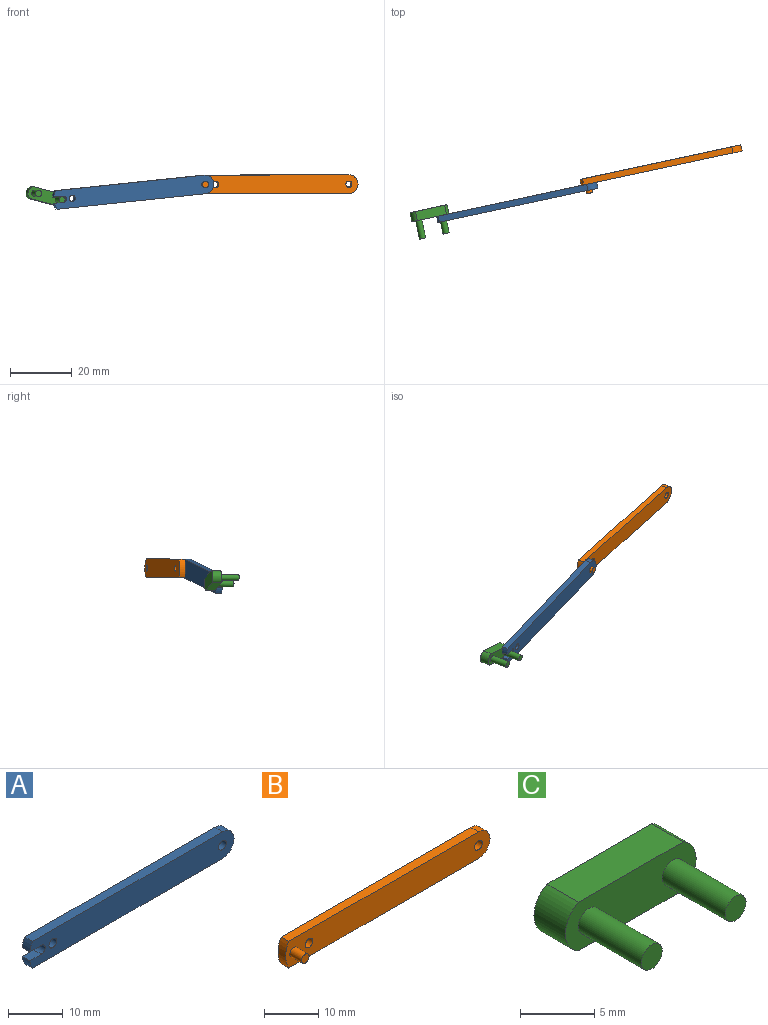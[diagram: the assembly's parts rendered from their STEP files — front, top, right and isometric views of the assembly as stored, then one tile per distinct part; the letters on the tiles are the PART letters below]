
ASSEMBLY  parts=3 mates=2
PART A: 12 faces, bbox 53x2x6 mm
  f0: cylinder r=1mm len=2mm, axis (0,1,0), area 6.3mm2, adj f1,f8,f10,f11
  f1: plane 3x2mm, normal (0,0,1), area 6mm2, adj f0,f2,f10,f11
  f2: cylinder r=6.08mm len=2mm, axis (0,1,0), area 4.3mm2, adj f1,f3,f10,f11
  f3: plane 49.29x2mm, normal (0,0,-1), area 98.6mm2, adj f2,f4,f10,f11
  f4: cylinder r=3mm len=6mm, axis (0,1,0), area 18.8mm2, adj f3,f5,f10,f11
  f5: plane 49.29x2mm, normal (0,0,1), area 98.6mm2, adj f4,f6,f10,f11
  f6: cylinder r=6.08mm len=2mm, axis (0,1,0), area 4.3mm2, adj f5,f8,f10,f11
  f7: cylinder r=1mm len=2mm, axis (0,1,0), area 12.6mm2, adj f10,f11
  f8: plane 3x2mm, normal (0,0,-1), area 6mm2, adj f0,f6,f10,f11
  f9: cylinder r=1mm len=2mm, axis (0,1,0), area 12.6mm2, adj f10,f11
  f10: plane 53x6mm, normal (0,-1,0), area 299.1mm2, adj f0,f1,f2,f3,f4,f5,f6,f7
  f11: plane 53x6mm, normal (0,1,0), area 299.1mm2, adj f0,f1,f2,f3,f4,f5,f6,f7
PART B: 10 faces, bbox 53.1x5x6 mm
  f0: cylinder r=6.08mm len=6mm, axis (0,1,0), area 12.5mm2, adj f1,f5,f6,f7
  f1: plane 49.29x2mm, normal (0,0,-1), area 98.6mm2, adj f0,f2,f6,f7
  f2: cylinder r=3mm len=6mm, axis (0,1,0), area 18.8mm2, adj f1,f5,f6,f7
  f3: cylinder r=1mm len=2mm, axis (0,1,0), area 12.6mm2, adj f6,f7
  f4: cylinder r=1mm len=2mm, axis (0,1,0), area 12.6mm2, adj f6,f7
  f5: plane 49.29x2mm, normal (0,0,1), area 98.6mm2, adj f0,f2,f6,f7
  f6: plane 53.08x6mm, normal (0,-1,0), area 303.7mm2, adj f0,f1,f2,f3,f4,f5,f8
  f7: plane 53.08x6mm, normal (0,1,0), area 306.8mm2, adj f0,f1,f2,f3,f4,f5
  f8: cylinder r=1mm len=3mm, axis (0,1,0), area 18.8mm2, adj f6,f9
  f9: plane 2x2mm, normal (0,-1,0), area 3.1mm2, adj f8
PART C: 10 faces, bbox 12.5x9x4 mm
  f0: plane 10x3mm, normal (0,0,-1), area 30mm2, adj f2,f3,f8,f9
  f1: plane 10x3mm, normal (0,0,1), area 30mm2, adj f2,f3,f8,f9
  f2: plane 12.47x4mm, normal (0,-1,0), area 40.8mm2, adj f0,f1,f4,f6,f8,f9
  f3: plane 12.47x4mm, normal (0,1,0), area 47.1mm2, adj f0,f1,f8,f9
  f4: cylinder r=1mm len=6mm, axis (0,1,0), area 37.7mm2, adj f2,f5
  f5: plane 2x2mm, normal (0,-1,0), area 3.1mm2, adj f4
  f6: cylinder r=1mm len=6mm, axis (0,1,0), area 37.7mm2, adj f2,f7
  f7: plane 2x2mm, normal (0,-1,0), area 3.1mm2, adj f6
  f8: cylinder r=2.24mm len=4mm, axis (0,-1,0), area 14.9mm2, adj f0,f1,f2,f3
  f9: cylinder r=2.24mm len=4mm, axis (0,-1,0), area 14.9mm2, adj f0,f1,f2,f3
PLACE A rot(axis=(0.08,-0.43,0.9),13.4deg) t=(-3.42,20.02,-1.28)mm
PLACE B rot(axis=(0.04,0,1),12.1deg) t=(43.38,32.11,-1.16)mm
PLACE C rot(axis=(0.11,-0.99,0.01),165.6deg) t=(-49.28,13.3,-7.45)mm
MATE pin_slot C.f4 <-> A.f0  axis (-0.21,0.98,0.01) through (-50.09,10.07,-9.17)mm
MATE revolute B.f8 <-> A.f9  axis (-0.21,0.98,0.01) through (-3.13,20.11,-4.27)mm
